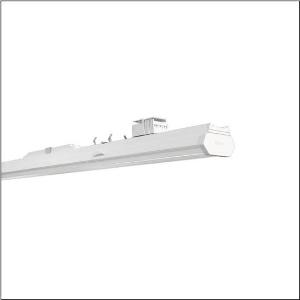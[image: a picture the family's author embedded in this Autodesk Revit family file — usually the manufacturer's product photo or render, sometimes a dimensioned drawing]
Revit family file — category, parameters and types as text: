
# Revit family: licross_11_protected_mo_51td12dn495g3c
name_source: partatom
category: Lighting Fixtures
units: mm (PartAtom-declared; Revit-internal decimal feet)

## family parameters
Cut with Voids When Loaded = No
Host = Face
Light Source = No
Part Type = Normal
Room Calculation Point = No
Round Connector Dimension = Use Diameter
Shared = No

## types (1)
- --- (1 x LED, 980 lm, 6.8 W, 4000K)
    Apparent Load = 7 VA
    CIE Flux Codes = 73 92 98 99 100
    Color Rendering = 80
    Color Temperature = 4000K
    Default Elevation = 1800 mm
    Description = Licross 11 Protected MO, luminaire insert, of sheet steel, galvanised, coil coated, white, length: 1.500mm, width: 90mm, height: 101mm, LED rated luminous flux: 9.980lm, light colour: 840, SDCM (Standard Deviation of Colour Matching)MacAdam ≤ 2 SDCM (initial), control gear: DALI 2 (for two DALI lines), with plug, 6-pole, with phase selection, for trunking rail, 14-core, mains connection: 220..240V, AC, 50/60Hz, rated input power: 61W, for trunking rail, 14-core, internal wiring halogen-free, for emergency light function, converter,control gear: single battery element, battery: LiFePO4, 9Ah, primary light control with lens, of plastic, primary optical cover: cover, of PMMA, light emission: direct distribution, primary light characteristic: symmetric, protection rating (complete): IP54, insulation class (complete): insulation class I (protective earthing), certification: CE, UKCA, protection symbol: D if used in an environment with non-conductive dust loads with corresponding accessories, impact resistance: IK06, permissible ambient temperature for indoor applications: +5..+35°C, standard: EN 60598-2-22, LABS conformity tested according to VDMA 24364:2018-05, reducing of maximum allowable ambient temperature of 5°C with ceiling mounting, corresponds to IFS (International Featured Standards) requirements for safety and quality in the food industry, The light source and the operating device comply with the requirements of the Ecodesign Regulation (EU) 2019/2020 and are replaceable in accordance with this regulation, packaging unit: 1 piece
    Height = 92 mm
    Lamp = 1 x LED
    Lamp Light Flux = 980 lm
    Lamp Power = 6.8 W
    Lamp count = 1
    Length = 1500 mm
    Luminous efficacy = 144 lm/W
    Manufacturer = Siteco
    ModVariant = No
    Model = 51TD12DN495G3C
    Mounting Place = Ceiling
    Mounting Type = Pendant
    Number of Poles = 1
    OnlyDefault = Yes
    Power Factor = 1
    Product Name = Licross 11 Protected MO
    Product group = luminaire insert | ceiling pendant
    ProductGroupID = 901
    Protection Class = Protection class I
    Protection Degree = IP 54
    RLX_Detail_Level = 1
    RLX_Emergency_Light_Flux = 0 lm
    RLX_Emergency_Type = 0
    RLX_Emergency_Type_DB = No
    RlxData = <blob elided: 25005 chars, md5=869bf858>
    Socket = socket
    Standby Power = 0 W
    System Light Flux = 980 lm
    System Power = 7 W
    Type Comments = : emergency light operation: 3 h
    Type Image = l_1256145.jpg
    URL = http://relux.com
    VarID = @adj_096081
    Voltage = 0 V
    Weight = 0.00 kg
    Width = 88 mm

## geometry (parser evidence)
native form markers: Blend x4, Sweep x10
no freeform markers — native parametric forms only
